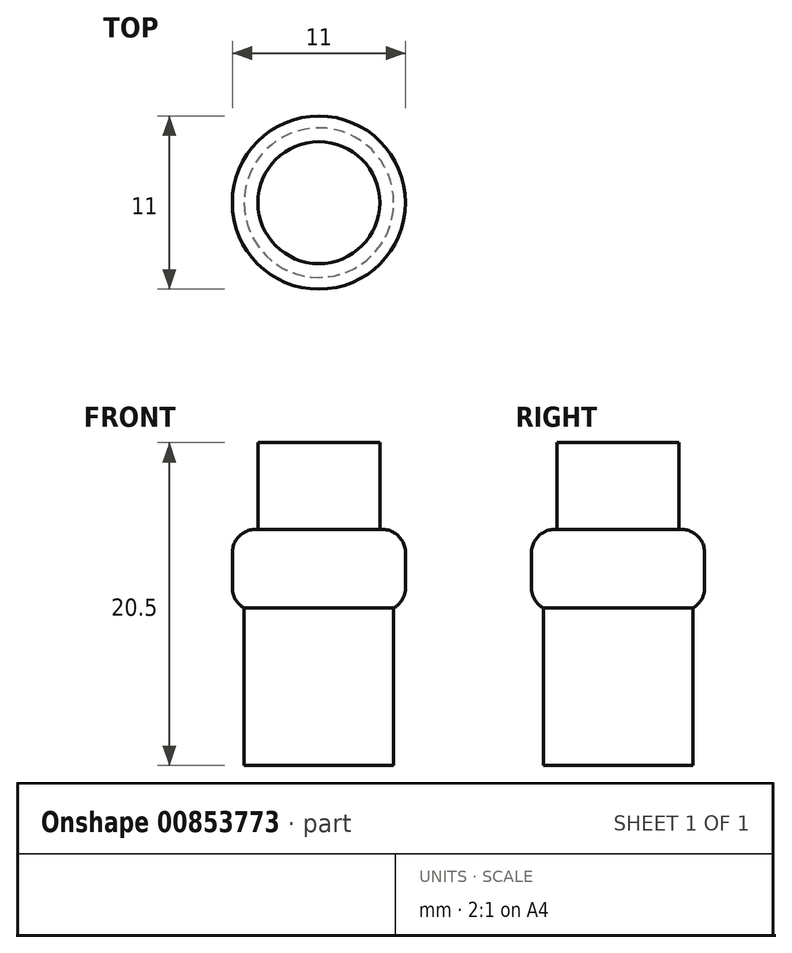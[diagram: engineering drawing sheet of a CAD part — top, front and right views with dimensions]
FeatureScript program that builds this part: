
annotation { "Feature Type Name" : "Feature", "Feature Type Description" : "" }
export const myFeature = defineFeature(function(context is Context, id is Id, definition is map)
    precondition{}
    {
        {
            var Q0;
            Q0=qCreatedBy(makeId("Top.planeOp"),FACE);
            var sketch = newSketch(context, id + "F0", { "sketchPlane" : qUnion([Q0])});
            skCircle(sketch, "E0", {"center": v(0, 0) * mm, "radius": 4.75 * mm});
            skSolve(sketch);
        }
        {
            var Q0;
            Q0 = qSketchRegion(id + "F0", true);
            extrude(context, id + "F1", {"entities" : qUnion([Q0]), "depth" : 10 * mm, "offsetDistance" : 25 * mm});
        }
        {
            var Q0;
            Q0=makeQuery(id+"F1.opExtrude","CAP_FACE",FACE,{"disambiguationData":[OSD([sQuery(id+"F0.wireOp",EDGE,"E0")])],"isStart":false});
            var sketch = newSketch(context, id + "F2", { "sketchPlane" : qUnion([Q0])});
            skCircle(sketch, "E1", {"center": v(0, 0) * mm, "radius": 5.5 * mm});
            skSolve(sketch);
        }
        {
            var Q0;
            Q0 = qSketchRegion(id + "F2", true);
            extrude(context, id + "F3", {"entities" : qUnion([Q0]), "operationType" : NewBodyOperationType.ADD, "depth" : 5 * mm, "offsetDistance" : 25 * mm});
        }
        {
            var Q0;
            Q0=makeQuery(id+"F3.opExtrude","CAP_FACE",FACE,{"disambiguationData":[OSD([sQuery(id+"F2.wireOp",EDGE,"E1")])],"isStart":false});
            var sketch = newSketch(context, id + "F4", { "sketchPlane" : qUnion([Q0])});
            skCircle(sketch, "E2", {"center": v(0, 0) * mm, "radius": 3.88 * mm});
            skSolve(sketch);
        }
        {
            var Q0;
            Q0 = qSketchRegion(id + "F4", true);
            extrude(context, id + "F5", {"entities" : qUnion([Q0]), "operationType" : NewBodyOperationType.ADD, "depth" : 5.5 * mm, "offsetDistance" : 25 * mm});
        }
        {
            var Q0;
            Q0=makeQuery(id+"F3.opExtrude","CAP_EDGE",EDGE,{"disambiguationData":[OSD([sQuery(id+"F2.wireOp",EDGE,"E1")])],"isStart":false});
            var Q1;
            Q1=makeQuery(id+"F3.opExtrude","CAP_EDGE",EDGE,{"disambiguationData":[OSD([sQuery(id+"F2.wireOp",EDGE,"E1")])],"isStart":true});
            fillet(context, id + "F6", {"entities" : qUnion([Q0, Q1]), "radius" : 1.5 * mm, "tangentPropagation" : true, "allowEdgeOverflow" : false});
        }
    });
